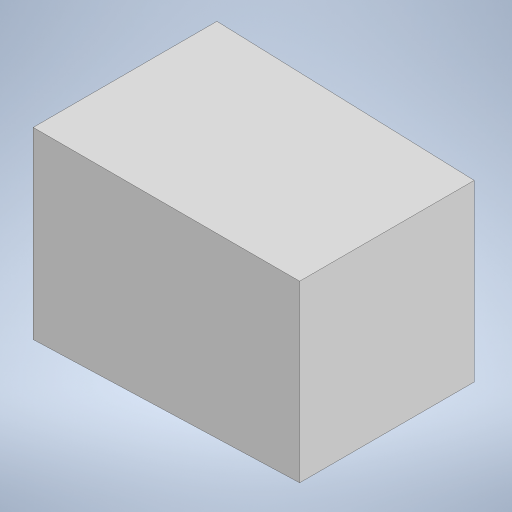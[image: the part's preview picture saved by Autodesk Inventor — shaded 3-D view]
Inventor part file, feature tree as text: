
AUTODESK INVENTOR PART (.ipt)
format: ipt  version: 2023 (Build 270158000, 158)  size: 167,936 bytes
history: native  units: in
note: dims shown in document units (in); Inventor stores cm internally (conversion verified against a paired STEP export)
features: extrude x1, draft x1
ambient origin geometry x8: Origin, YZ Plane, XZ Plane, XY Plane, X Axis, Y Axis, Z Axis, Center Point
bodies: Solid1 (feature_tree)
feature tree (2):
  extrude  "Extrusion1"  TaperAngle=0.0deg  [1 undecoded]
  draft  "FaceDraft1"
note: 1 required parameter value undecoded (feature->parameter linkage not recoverable at this tier; creation-order binding heuristic only, values carry confidence <= 0.55)
